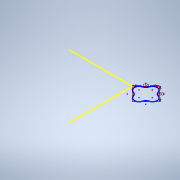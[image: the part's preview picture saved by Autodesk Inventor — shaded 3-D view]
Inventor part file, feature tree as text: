
AUTODESK INVENTOR PART (.ipt)
format: ipt  version: 2021 (Build 250183000, 183)  size: 94,208 bytes
history: native  units: in
note: dims shown in document units (in); Inventor stores cm internally (conversion verified against a paired STEP export)
features: sketch x1
ambient origin geometry x8: Origin, YZ Plane, XZ Plane, XY Plane, X Axis, Y Axis, Z Axis, Center Point
feature tree (1):
  sketch  "Boceto1"  dims[d4=5.9055in d5=5.9055in]
